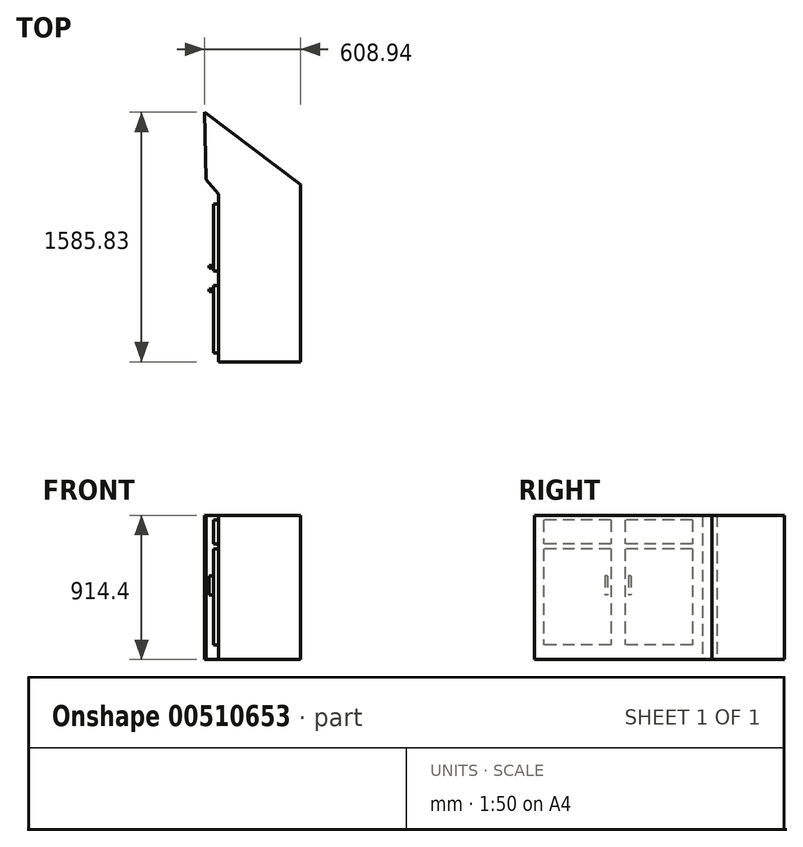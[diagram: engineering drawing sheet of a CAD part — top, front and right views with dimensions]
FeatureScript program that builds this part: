
annotation { "Feature Type Name" : "Feature", "Feature Type Description" : "" }
export const myFeature = defineFeature(function(context is Context, id is Id, definition is map)
    precondition{}
    {
        {
            var Q0;
            Q0=qCreatedBy(makeId("Top.planeOp"),FACE);
            var sketch = newSketch(context, id + "F0", { "sketchPlane" : qUnion([Q0])});
            skLineSegment(sketch, "E0", {"start": v(-290.51, 651.1) * mm, "end": v(318.43, 193.02) * mm});
            skLineSegment(sketch, "E1", {"start": v(318.43, 193.02) * mm, "end": v(318.43, -934.74) * mm});
            skLineSegment(sketch, "E2", {"start": v(318.43, -934.74) * mm, "end": v(-201.23, -934.74) * mm});
            skLineSegment(sketch, "E3", {"start": v(-201.23, -934.74) * mm, "end": v(-201.23, 132.06) * mm});
            skLineSegment(sketch, "E4", {"start": v(-201.23, 132.06) * mm, "end": v(-280.74, 224.49) * mm});
            skLineSegment(sketch, "E5", {"start": v(-280.74, 224.49) * mm, "end": v(-290.51, 651.1) * mm});
            skSolve(sketch);
        }
        {
            var Q0;
            Q0 = qSketchRegion(id + "F0", true);
            extrude(context, id + "F1", {"entities" : qUnion([Q0]), "depth" : 914.4 * mm, "offsetDistance" : 30.48 * mm});
        }
        {
            var Q0;
            Q0=makeQuery(id+"F1.opExtrude","SWEPT_FACE",FACE,{"disambiguationData":[OSD([sQuery(id+"F0.wireOp",EDGE,"E3")])]});
            var sketch = newSketch(context, id + "F2", { "sketchPlane" : qUnion([Q0])});
            skLineSegment(sketch, "E6.bottom", {"start": v(-68.05, 701.04) * mm, "end": v(358.67, 701.04) * mm});
            skLineSegment(sketch, "E6.top", {"start": v(-68.05, 91.44) * mm, "end": v(358.67, 91.44) * mm});
            skLineSegment(sketch, "E6.left", {"start": v(-68.05, 701.04) * mm, "end": v(-68.05, 91.44) * mm});
            skLineSegment(sketch, "E6.right", {"start": v(358.67, 701.04) * mm, "end": v(358.67, 91.44) * mm});
            skLineSegment(sketch, "E7.bottom", {"start": v(450.1, 701.04) * mm, "end": v(876.83, 701.04) * mm});
            skLineSegment(sketch, "E7.top", {"start": v(450.1, 91.44) * mm, "end": v(876.83, 91.44) * mm});
            skLineSegment(sketch, "E7.left", {"start": v(450.1, 701.04) * mm, "end": v(450.1, 91.44) * mm});
            skLineSegment(sketch, "E7.right", {"start": v(876.83, 701.04) * mm, "end": v(876.83, 91.44) * mm});
            skLineSegment(sketch, "E8.bottom", {"start": v(-68.05, 883.92) * mm, "end": v(358.67, 883.92) * mm});
            skLineSegment(sketch, "E8.top", {"start": v(-68.05, 731.52) * mm, "end": v(358.67, 731.52) * mm});
            skLineSegment(sketch, "E8.left", {"start": v(-68.05, 883.92) * mm, "end": v(-68.05, 731.52) * mm});
            skLineSegment(sketch, "E8.right", {"start": v(358.67, 883.92) * mm, "end": v(358.67, 731.52) * mm});
            skLineSegment(sketch, "E9.bottom", {"start": v(450.1, 883.92) * mm, "end": v(876.83, 883.92) * mm});
            skLineSegment(sketch, "E9.top", {"start": v(450.1, 731.52) * mm, "end": v(876.83, 731.52) * mm});
            skLineSegment(sketch, "E9.left", {"start": v(450.1, 883.92) * mm, "end": v(450.1, 731.52) * mm});
            skLineSegment(sketch, "E9.right", {"start": v(876.83, 883.92) * mm, "end": v(876.83, 731.52) * mm});
            skSolve(sketch);
        }
        {
            var Q0;
            Q0 = qSketchRegion(id + "F2", true);
            extrude(context, id + "F3", {"entities" : qUnion([Q0]), "operationType" : NewBodyOperationType.ADD, "depth" : 30.48 * mm, "offsetDistance" : 30.48 * mm});
        }
        {
            var Q0;
            Q0=makeQuery(id+"F3.opExtrude","CAP_FACE",FACE,{"disambiguationData":[OSD([sQuery(id+"F2.wireOp",EDGE,"E6.bottom"),sQuery(id+"F2.wireOp",EDGE,"E6.top"),sQuery(id+"F2.wireOp",EDGE,"E6.left"),sQuery(id+"F2.wireOp",EDGE,"E6.right")])],"isStart":false});
            var sketch = newSketch(context, id + "F4", { "sketchPlane" : qUnion([Q0])});
            skLineSegment(sketch, "E10.bottom", {"start": v(322.1, 530.96) * mm, "end": v(337.33, 530.96) * mm});
            skLineSegment(sketch, "E10.top", {"start": v(322.1, 409.04) * mm, "end": v(337.33, 409.04) * mm});
            skLineSegment(sketch, "E10.left", {"start": v(322.1, 530.96) * mm, "end": v(322.1, 409.04) * mm});
            skLineSegment(sketch, "E10.right", {"start": v(337.33, 530.96) * mm, "end": v(337.33, 409.04) * mm});
            skLineSegment(sketch, "E11.bottom", {"start": v(471.44, 530.96) * mm, "end": v(486.68, 530.96) * mm});
            skLineSegment(sketch, "E11.top", {"start": v(471.44, 409.04) * mm, "end": v(486.68, 409.04) * mm});
            skLineSegment(sketch, "E11.left", {"start": v(471.44, 530.96) * mm, "end": v(471.44, 409.04) * mm});
            skLineSegment(sketch, "E11.right", {"start": v(486.68, 530.96) * mm, "end": v(486.68, 409.04) * mm});
            skSolve(sketch);
        }
        {
            var Q0;
            Q0 = qSketchRegion(id + "F4", true);
            extrude(context, id + "F5", {"entities" : qUnion([Q0]), "operationType" : NewBodyOperationType.ADD, "depth" : 30.48 * mm, "offsetDistance" : 30.48 * mm});
        }
    });
